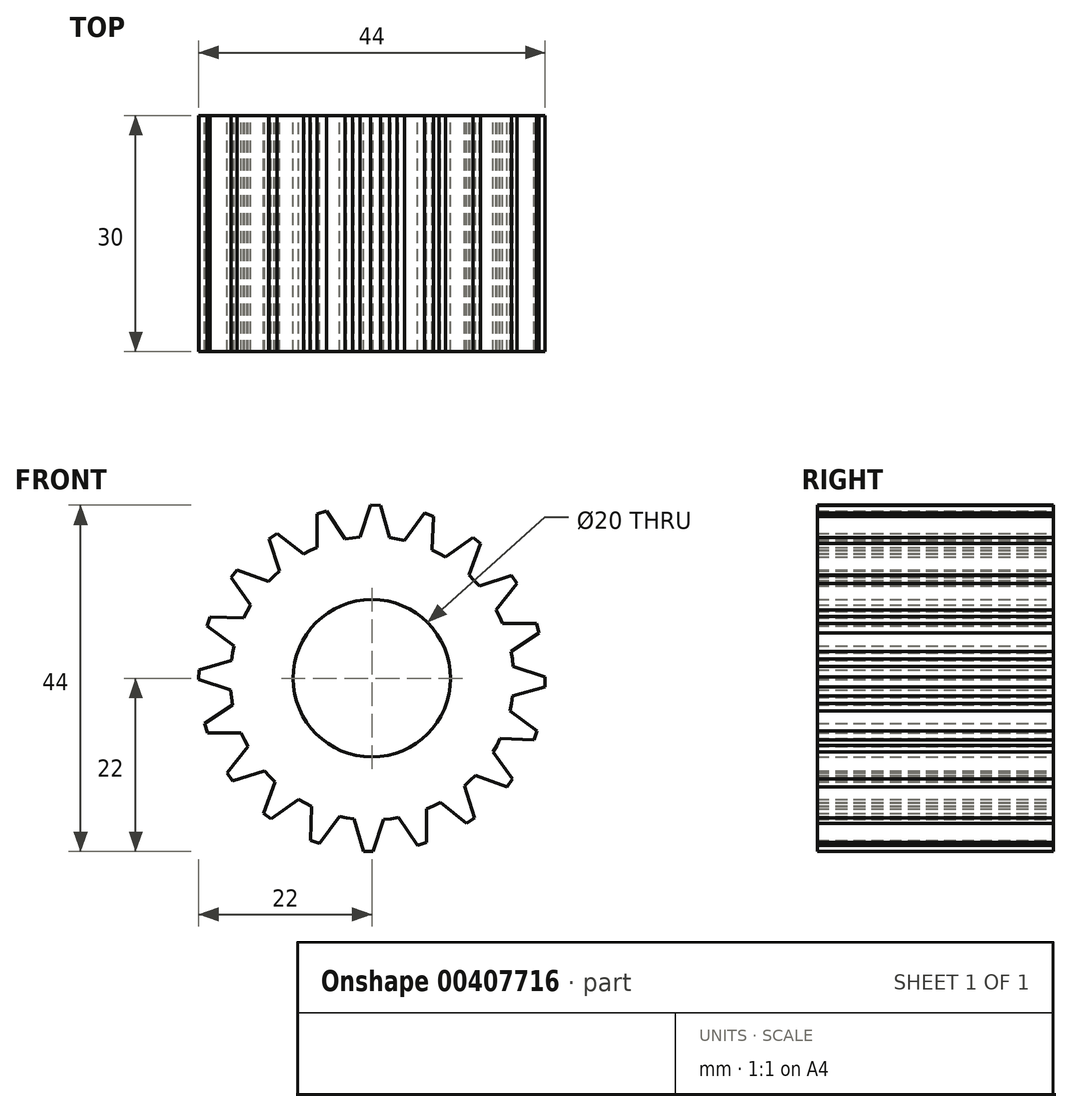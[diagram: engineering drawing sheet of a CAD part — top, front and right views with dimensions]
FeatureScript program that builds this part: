
annotation { "Feature Type Name" : "Feature", "Feature Type Description" : "" }
export const myFeature = defineFeature(function(context is Context, id is Id, definition is map)
    precondition{}
    {
        {
            var Q0;
            Q0=qCreatedBy(makeId("Front.planeOp"),FACE);
            var sketch = newSketch(context, id + "F0", { "sketchPlane" : qUnion([Q0])});
            skArc(sketch, "E0", {"start": v(5.4, 19.26) * mm, "mid": v(5.24, 19.3) * mm, "end": v(5.08, 19.34) * mm, "construction": true});
            skPoint(sketch, "E1", {"position": v(3.2, 17.71) * mm});
            skPoint(sketch, "E2", {"position": v(4.13, 17.52) * mm});
            skPoint(sketch, "E3", {"position": v(6.66, 20.97) * mm});
            skPoint(sketch, "E4", {"position": v(7.81, 20.57) * mm});
            skPoint(sketch, "E5", {"position": v(7.65, 16.3) * mm});
            skPoint(sketch, "E6", {"position": v(8.5, 15.86) * mm});
            skLineSegment(sketch, "E7", {"start": v(3.2, 17.71) * mm, "end": v(4.13, 17.52) * mm});
            skLineSegment(sketch, "E8", {"start": v(4.13, 17.52) * mm, "end": v(6.66, 20.97) * mm});
            skLineSegment(sketch, "E9", {"start": v(6.66, 20.97) * mm, "end": v(7.81, 20.57) * mm});
            skLineSegment(sketch, "E10", {"start": v(7.81, 20.57) * mm, "end": v(7.65, 16.3) * mm});
            skLineSegment(sketch, "E11", {"start": v(7.65, 16.3) * mm, "end": v(8.5, 15.86) * mm});
            skLineSegment(sketch, "E12.1.0", {"start": v(-2.44, 17.83) * mm, "end": v(-1.48, 17.94) * mm});
            skLineSegment(sketch, "E12.1.1", {"start": v(-1.48, 17.94) * mm, "end": v(-0.15, 22) * mm});
            skLineSegment(sketch, "E12.1.2", {"start": v(-0.15, 22) * mm, "end": v(1.08, 21.97) * mm});
            skLineSegment(sketch, "E12.1.3", {"start": v(1.08, 21.97) * mm, "end": v(2.24, 17.86) * mm});
            skLineSegment(sketch, "E12.1.4", {"start": v(2.24, 17.86) * mm, "end": v(3.2, 17.71) * mm});
            skLineSegment(sketch, "E12.2.0", {"start": v(-7.83, 16.2) * mm, "end": v(-6.95, 16.6) * mm});
            skLineSegment(sketch, "E12.2.1", {"start": v(-6.95, 16.6) * mm, "end": v(-6.94, 20.88) * mm});
            skLineSegment(sketch, "E12.2.2", {"start": v(-6.94, 20.88) * mm, "end": v(-5.77, 21.23) * mm});
            skLineSegment(sketch, "E12.2.3", {"start": v(-5.77, 21.23) * mm, "end": v(-3.39, 17.68) * mm});
            skLineSegment(sketch, "E12.2.4", {"start": v(-3.39, 17.68) * mm, "end": v(-2.44, 17.83) * mm});
            skLineSegment(sketch, "E12.3.0", {"start": v(-12.46, 13) * mm, "end": v(-11.74, 13.64) * mm});
            skLineSegment(sketch, "E12.3.1", {"start": v(-11.74, 13.64) * mm, "end": v(-13.05, 17.71) * mm});
            skLineSegment(sketch, "E12.3.2", {"start": v(-13.05, 17.71) * mm, "end": v(-12.04, 18.41) * mm});
            skLineSegment(sketch, "E12.3.3", {"start": v(-12.04, 18.41) * mm, "end": v(-8.69, 15.77) * mm});
            skLineSegment(sketch, "E12.3.4", {"start": v(-8.69, 15.77) * mm, "end": v(-7.83, 16.2) * mm});
            skLineSegment(sketch, "E12.4.0", {"start": v(-15.86, 8.5) * mm, "end": v(-15.38, 9.34) * mm});
            skLineSegment(sketch, "E12.4.1", {"start": v(-15.38, 9.34) * mm, "end": v(-17.89, 12.81) * mm});
            skLineSegment(sketch, "E12.4.2", {"start": v(-17.89, 12.81) * mm, "end": v(-17.14, 13.79) * mm});
            skLineSegment(sketch, "E12.4.3", {"start": v(-17.14, 13.79) * mm, "end": v(-13.13, 12.3) * mm});
            skLineSegment(sketch, "E12.4.4", {"start": v(-13.13, 12.3) * mm, "end": v(-12.46, 13) * mm});
            skLineSegment(sketch, "E12.5.0", {"start": v(-17.71, 3.2) * mm, "end": v(-17.52, 4.13) * mm});
            skLineSegment(sketch, "E12.5.1", {"start": v(-17.52, 4.13) * mm, "end": v(-20.97, 6.66) * mm});
            skLineSegment(sketch, "E12.5.2", {"start": v(-20.97, 6.66) * mm, "end": v(-20.57, 7.81) * mm});
            skLineSegment(sketch, "E12.5.3", {"start": v(-20.57, 7.81) * mm, "end": v(-16.3, 7.65) * mm});
            skLineSegment(sketch, "E12.5.4", {"start": v(-16.3, 7.65) * mm, "end": v(-15.86, 8.5) * mm});
            skLineSegment(sketch, "E12.6.0", {"start": v(-17.83, -2.44) * mm, "end": v(-17.94, -1.48) * mm});
            skLineSegment(sketch, "E12.6.1", {"start": v(-17.94, -1.48) * mm, "end": v(-22, -0.15) * mm});
            skLineSegment(sketch, "E12.6.2", {"start": v(-22, -0.15) * mm, "end": v(-21.97, 1.08) * mm});
            skLineSegment(sketch, "E12.6.3", {"start": v(-21.97, 1.08) * mm, "end": v(-17.86, 2.24) * mm});
            skLineSegment(sketch, "E12.6.4", {"start": v(-17.86, 2.24) * mm, "end": v(-17.71, 3.2) * mm});
            skLineSegment(sketch, "E12.7.0", {"start": v(-16.2, -7.83) * mm, "end": v(-16.6, -6.95) * mm});
            skLineSegment(sketch, "E12.7.1", {"start": v(-16.6, -6.95) * mm, "end": v(-20.88, -6.94) * mm});
            skLineSegment(sketch, "E12.7.2", {"start": v(-20.88, -6.94) * mm, "end": v(-21.23, -5.77) * mm});
            skLineSegment(sketch, "E12.7.3", {"start": v(-21.23, -5.77) * mm, "end": v(-17.68, -3.39) * mm});
            skLineSegment(sketch, "E12.7.4", {"start": v(-17.68, -3.39) * mm, "end": v(-17.83, -2.44) * mm});
            skLineSegment(sketch, "E12.8.0", {"start": v(-13, -12.46) * mm, "end": v(-13.64, -11.74) * mm});
            skLineSegment(sketch, "E12.8.1", {"start": v(-13.64, -11.74) * mm, "end": v(-17.71, -13.05) * mm});
            skLineSegment(sketch, "E12.8.2", {"start": v(-17.71, -13.05) * mm, "end": v(-18.41, -12.04) * mm});
            skLineSegment(sketch, "E12.8.3", {"start": v(-18.41, -12.04) * mm, "end": v(-15.77, -8.69) * mm});
            skLineSegment(sketch, "E12.8.4", {"start": v(-15.77, -8.69) * mm, "end": v(-16.2, -7.83) * mm});
            skLineSegment(sketch, "E12.9.0", {"start": v(-8.5, -15.86) * mm, "end": v(-9.34, -15.38) * mm});
            skLineSegment(sketch, "E12.9.1", {"start": v(-9.34, -15.38) * mm, "end": v(-12.81, -17.89) * mm});
            skLineSegment(sketch, "E12.9.2", {"start": v(-12.81, -17.89) * mm, "end": v(-13.79, -17.14) * mm});
            skLineSegment(sketch, "E12.9.3", {"start": v(-13.79, -17.14) * mm, "end": v(-12.3, -13.13) * mm});
            skLineSegment(sketch, "E12.9.4", {"start": v(-12.3, -13.13) * mm, "end": v(-13, -12.46) * mm});
            skLineSegment(sketch, "E12.10.0", {"start": v(-3.2, -17.71) * mm, "end": v(-4.13, -17.52) * mm});
            skLineSegment(sketch, "E12.10.1", {"start": v(-4.13, -17.52) * mm, "end": v(-6.66, -20.97) * mm});
            skLineSegment(sketch, "E12.10.2", {"start": v(-6.66, -20.97) * mm, "end": v(-7.81, -20.57) * mm});
            skLineSegment(sketch, "E12.10.3", {"start": v(-7.81, -20.57) * mm, "end": v(-7.65, -16.3) * mm});
            skLineSegment(sketch, "E12.10.4", {"start": v(-7.65, -16.3) * mm, "end": v(-8.5, -15.86) * mm});
            skLineSegment(sketch, "E12.11.0", {"start": v(2.44, -17.83) * mm, "end": v(1.48, -17.94) * mm});
            skLineSegment(sketch, "E12.11.1", {"start": v(1.48, -17.94) * mm, "end": v(0.15, -22) * mm});
            skLineSegment(sketch, "E12.11.2", {"start": v(0.15, -22) * mm, "end": v(-1.08, -21.97) * mm});
            skLineSegment(sketch, "E12.11.3", {"start": v(-1.08, -21.97) * mm, "end": v(-2.24, -17.86) * mm});
            skLineSegment(sketch, "E12.11.4", {"start": v(-2.24, -17.86) * mm, "end": v(-3.2, -17.71) * mm});
            skLineSegment(sketch, "E12.12.0", {"start": v(7.83, -16.2) * mm, "end": v(6.95, -16.6) * mm});
            skLineSegment(sketch, "E12.12.1", {"start": v(6.95, -16.6) * mm, "end": v(6.94, -20.88) * mm});
            skLineSegment(sketch, "E12.12.2", {"start": v(6.94, -20.88) * mm, "end": v(5.77, -21.23) * mm});
            skLineSegment(sketch, "E12.12.3", {"start": v(5.77, -21.23) * mm, "end": v(3.39, -17.68) * mm});
            skLineSegment(sketch, "E12.12.4", {"start": v(3.39, -17.68) * mm, "end": v(2.44, -17.83) * mm});
            skLineSegment(sketch, "E12.13.0", {"start": v(12.46, -13) * mm, "end": v(11.74, -13.64) * mm});
            skLineSegment(sketch, "E12.13.1", {"start": v(11.74, -13.64) * mm, "end": v(13.05, -17.71) * mm});
            skLineSegment(sketch, "E12.13.2", {"start": v(13.05, -17.71) * mm, "end": v(12.04, -18.41) * mm});
            skLineSegment(sketch, "E12.13.3", {"start": v(12.04, -18.41) * mm, "end": v(8.69, -15.77) * mm});
            skLineSegment(sketch, "E12.13.4", {"start": v(8.69, -15.77) * mm, "end": v(7.83, -16.2) * mm});
            skLineSegment(sketch, "E12.14.0", {"start": v(15.86, -8.5) * mm, "end": v(15.38, -9.34) * mm});
            skLineSegment(sketch, "E12.14.1", {"start": v(15.38, -9.34) * mm, "end": v(17.89, -12.81) * mm});
            skLineSegment(sketch, "E12.14.2", {"start": v(17.89, -12.81) * mm, "end": v(17.14, -13.79) * mm});
            skLineSegment(sketch, "E12.14.3", {"start": v(17.14, -13.79) * mm, "end": v(13.13, -12.3) * mm});
            skLineSegment(sketch, "E12.14.4", {"start": v(13.13, -12.3) * mm, "end": v(12.46, -13) * mm});
            skLineSegment(sketch, "E12.15.0", {"start": v(17.71, -3.2) * mm, "end": v(17.52, -4.13) * mm});
            skLineSegment(sketch, "E12.15.1", {"start": v(17.52, -4.13) * mm, "end": v(20.97, -6.66) * mm});
            skLineSegment(sketch, "E12.15.2", {"start": v(20.97, -6.66) * mm, "end": v(20.57, -7.81) * mm});
            skLineSegment(sketch, "E12.15.3", {"start": v(20.57, -7.81) * mm, "end": v(16.3, -7.65) * mm});
            skLineSegment(sketch, "E12.15.4", {"start": v(16.3, -7.65) * mm, "end": v(15.86, -8.5) * mm});
            skLineSegment(sketch, "E12.16.0", {"start": v(17.83, 2.44) * mm, "end": v(17.94, 1.48) * mm});
            skLineSegment(sketch, "E12.16.1", {"start": v(17.94, 1.48) * mm, "end": v(22, 0.15) * mm});
            skLineSegment(sketch, "E12.16.2", {"start": v(22, 0.15) * mm, "end": v(21.97, -1.08) * mm});
            skLineSegment(sketch, "E12.16.3", {"start": v(21.97, -1.08) * mm, "end": v(17.86, -2.24) * mm});
            skLineSegment(sketch, "E12.16.4", {"start": v(17.86, -2.24) * mm, "end": v(17.71, -3.2) * mm});
            skLineSegment(sketch, "E12.17.0", {"start": v(16.2, 7.83) * mm, "end": v(16.6, 6.95) * mm});
            skLineSegment(sketch, "E12.17.1", {"start": v(16.6, 6.95) * mm, "end": v(20.88, 6.94) * mm});
            skLineSegment(sketch, "E12.17.2", {"start": v(20.88, 6.94) * mm, "end": v(21.23, 5.77) * mm});
            skLineSegment(sketch, "E12.17.3", {"start": v(21.23, 5.77) * mm, "end": v(17.68, 3.39) * mm});
            skLineSegment(sketch, "E12.17.4", {"start": v(17.68, 3.39) * mm, "end": v(17.83, 2.44) * mm});
            skLineSegment(sketch, "E12.18.0", {"start": v(13, 12.46) * mm, "end": v(13.64, 11.74) * mm});
            skLineSegment(sketch, "E12.18.1", {"start": v(13.64, 11.74) * mm, "end": v(17.71, 13.05) * mm});
            skLineSegment(sketch, "E12.18.2", {"start": v(17.71, 13.05) * mm, "end": v(18.41, 12.04) * mm});
            skLineSegment(sketch, "E12.18.3", {"start": v(18.41, 12.04) * mm, "end": v(15.77, 8.69) * mm});
            skLineSegment(sketch, "E12.18.4", {"start": v(15.77, 8.69) * mm, "end": v(16.2, 7.83) * mm});
            skLineSegment(sketch, "E12.19.0", {"start": v(8.5, 15.86) * mm, "end": v(9.34, 15.38) * mm});
            skLineSegment(sketch, "E12.19.1", {"start": v(9.34, 15.38) * mm, "end": v(12.81, 17.89) * mm});
            skLineSegment(sketch, "E12.19.2", {"start": v(12.81, 17.89) * mm, "end": v(13.79, 17.14) * mm});
            skLineSegment(sketch, "E12.19.3", {"start": v(13.79, 17.14) * mm, "end": v(12.3, 13.13) * mm});
            skLineSegment(sketch, "E12.19.4", {"start": v(12.3, 13.13) * mm, "end": v(13, 12.46) * mm});
            skCircle(sketch, "E13", {"center": v(0, 0) * mm, "radius": 10 * mm});
            skSolve(sketch);
        }
        {
            var Q0;
            Q0=makeQuery(id+"F0.imprint","IMPRINT",FACE,{"disambiguationData":[TD([[makeQuery(id+"F0.imprint","IMPRINT",EDGE,{"derivedFrom":sQuery(id+"F0.wireOp",EDGE,"E7")}),-1.0]])]});
            extrude(context, id + "F1", {"entities" : qUnion([Q0]), "flatOperationType" : FlatOperationType.REMOVE, "offsetDistance" : 25.4 * mm, "depth" : 30 * mm, "domain" : OperationDomain.MODEL, "symmetric" : true});
        }
    });
